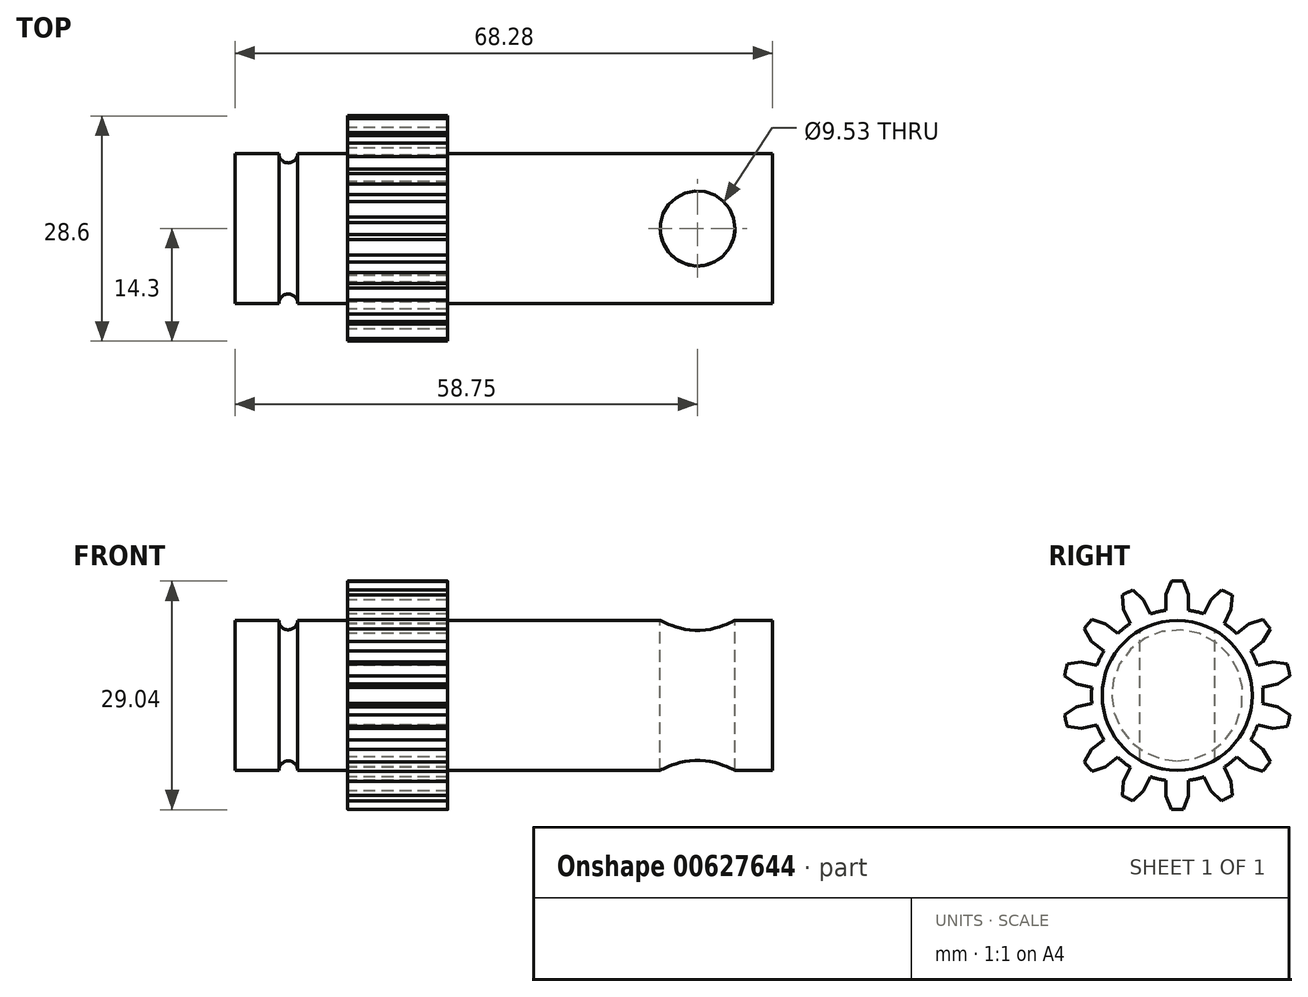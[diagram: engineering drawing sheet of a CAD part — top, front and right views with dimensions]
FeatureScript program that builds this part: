
annotation { "Feature Type Name" : "Feature", "Feature Type Description" : "" }
export const myFeature = defineFeature(function(context is Context, id is Id, definition is map)
    precondition{}
    {
        {
            var Q0;
            Q0=qCreatedBy(makeId("Right.planeOp"),FACE);
            var sketch = newSketch(context, id + "F0", { "sketchPlane" : qUnion([Q0])});
            skCircle(sketch, "E0", {"center": v(0, 0) * mm, "radius": 9.53 * mm});
            skSolve(sketch);
        }
        {
            var Q0;
            Q0 = qSketchRegion(id + "F0", true);
            extrude(context, id + "F1", {"entities" : qUnion([Q0]), "oppositeDirection" : true, "depth" : 14.3 * mm, "offsetDistance" : 25.4 * mm});
        }
        {
            var Q0;
            Q0=makeQuery(id+"F1.opExtrude","CAP_FACE",FACE,{"disambiguationData":[OSD([sQuery(id+"F0.wireOp",EDGE,"E0")])],"isStart":true});
            var sketch = newSketch(context, id + "F2", { "sketchPlane" : qUnion([Q0])});
            skArc(sketch, "E1", {"start": v(0.76, 14.5) * mm, "mid": v(0, 14.52) * mm, "end": v(-0.76, 14.5) * mm});
            skArc(sketch, "E2", {"start": v(-1.41, 10.8) * mm, "mid": v(-2.42, 10.62) * mm, "end": v(-3.41, 10.35) * mm, "construction": true});
            skLineSegment(sketch, "E3", {"start": v(-0.76, 14.5) * mm, "end": v(-1.41, 12.8) * mm});
            skLineSegment(sketch, "E4", {"start": v(-1.41, 12.8) * mm, "end": v(-1.41, 10.8) * mm});
            skLineSegment(sketch, "E5", {"start": v(0, 14.52) * mm, "end": v(0, 10.9) * mm, "construction": true});
            skLineSegment(sketch, "E6.MirrorCS", {"start": v(1.41, 12.8) * mm, "end": v(1.41, 10.8) * mm});
            skLineSegment(sketch, "E7.MirrorCS", {"start": v(0.76, 14.5) * mm, "end": v(1.41, 12.8) * mm});
            skLineSegment(sketch, "E8.1.0", {"start": v(-6.83, 10.92) * mm, "end": v(-5.96, 9.12) * mm});
            skLineSegment(sketch, "E8.1.1", {"start": v(-6.98, 12.73) * mm, "end": v(-6.83, 10.92) * mm});
            skArc(sketch, "E8.1.2", {"start": v(-5.6, 13.4) * mm, "mid": v(-6.3, 13.08) * mm, "end": v(-6.98, 12.73) * mm});
            skLineSegment(sketch, "E8.1.3", {"start": v(-5.6, 13.4) * mm, "end": v(-4.28, 12.14) * mm});
            skLineSegment(sketch, "E8.1.4", {"start": v(-4.28, 12.14) * mm, "end": v(-3.41, 10.35) * mm});
            skLineSegment(sketch, "E8.2.0", {"start": v(-10.89, 6.87) * mm, "end": v(-9.33, 5.63) * mm});
            skLineSegment(sketch, "E8.2.1", {"start": v(-11.8, 8.44) * mm, "end": v(-10.89, 6.87) * mm});
            skArc(sketch, "E8.2.2", {"start": v(-10.86, 9.63) * mm, "mid": v(-11.35, 9.05) * mm, "end": v(-11.8, 8.44) * mm});
            skLineSegment(sketch, "E8.2.3", {"start": v(-10.86, 9.63) * mm, "end": v(-9.13, 9.09) * mm});
            skLineSegment(sketch, "E8.2.4", {"start": v(-9.13, 9.09) * mm, "end": v(-7.57, 7.84) * mm});
            skLineSegment(sketch, "E8.3.0", {"start": v(-12.8, 1.47) * mm, "end": v(-10.85, 1.03) * mm});
            skLineSegment(sketch, "E8.3.1", {"start": v(-14.3, 2.48) * mm, "end": v(-12.8, 1.47) * mm});
            skArc(sketch, "E8.3.2", {"start": v(-13.96, 3.97) * mm, "mid": v(-14.15, 3.23) * mm, "end": v(-14.3, 2.48) * mm});
            skLineSegment(sketch, "E8.3.3", {"start": v(-13.96, 3.97) * mm, "end": v(-12.16, 4.23) * mm});
            skLineSegment(sketch, "E8.3.4", {"start": v(-12.16, 4.23) * mm, "end": v(-10.22, 3.78) * mm});
            skLineSegment(sketch, "E8.4.0", {"start": v(-12.16, -4.23) * mm, "end": v(-10.22, -3.78) * mm});
            skLineSegment(sketch, "E8.4.1", {"start": v(-13.96, -3.97) * mm, "end": v(-12.16, -4.23) * mm});
            skArc(sketch, "E8.4.2", {"start": v(-14.3, -2.48) * mm, "mid": v(-14.15, -3.23) * mm, "end": v(-13.96, -3.97) * mm});
            skLineSegment(sketch, "E8.4.3", {"start": v(-14.3, -2.48) * mm, "end": v(-12.8, -1.47) * mm});
            skLineSegment(sketch, "E8.4.4", {"start": v(-12.8, -1.47) * mm, "end": v(-10.85, -1.03) * mm});
            skLineSegment(sketch, "E8.5.0", {"start": v(-9.13, -9.09) * mm, "end": v(-7.57, -7.84) * mm});
            skLineSegment(sketch, "E8.5.1", {"start": v(-10.86, -9.63) * mm, "end": v(-9.13, -9.09) * mm});
            skArc(sketch, "E8.5.2", {"start": v(-11.8, -8.44) * mm, "mid": v(-11.35, -9.05) * mm, "end": v(-10.86, -9.63) * mm});
            skLineSegment(sketch, "E8.5.3", {"start": v(-11.8, -8.44) * mm, "end": v(-10.89, -6.87) * mm});
            skLineSegment(sketch, "E8.5.4", {"start": v(-10.89, -6.87) * mm, "end": v(-9.33, -5.63) * mm});
            skLineSegment(sketch, "E8.6.0", {"start": v(-4.28, -12.14) * mm, "end": v(-3.41, -10.35) * mm});
            skLineSegment(sketch, "E8.6.1", {"start": v(-5.6, -13.4) * mm, "end": v(-4.28, -12.14) * mm});
            skArc(sketch, "E8.6.2", {"start": v(-6.98, -12.73) * mm, "mid": v(-6.3, -13.08) * mm, "end": v(-5.6, -13.4) * mm});
            skLineSegment(sketch, "E8.6.3", {"start": v(-6.98, -12.73) * mm, "end": v(-6.83, -10.92) * mm});
            skLineSegment(sketch, "E8.6.4", {"start": v(-6.83, -10.92) * mm, "end": v(-5.96, -9.12) * mm});
            skLineSegment(sketch, "E8.7.0", {"start": v(1.41, -12.8) * mm, "end": v(1.41, -10.8) * mm});
            skLineSegment(sketch, "E8.7.1", {"start": v(0.76, -14.5) * mm, "end": v(1.41, -12.8) * mm});
            skArc(sketch, "E8.7.2", {"start": v(-0.76, -14.5) * mm, "mid": v(0, -14.52) * mm, "end": v(0.76, -14.5) * mm});
            skLineSegment(sketch, "E8.7.3", {"start": v(-0.76, -14.5) * mm, "end": v(-1.41, -12.8) * mm});
            skLineSegment(sketch, "E8.7.4", {"start": v(-1.41, -12.8) * mm, "end": v(-1.41, -10.8) * mm});
            skLineSegment(sketch, "E8.8.0", {"start": v(6.83, -10.92) * mm, "end": v(5.96, -9.12) * mm});
            skLineSegment(sketch, "E8.8.1", {"start": v(6.98, -12.73) * mm, "end": v(6.83, -10.92) * mm});
            skArc(sketch, "E8.8.2", {"start": v(5.6, -13.4) * mm, "mid": v(6.3, -13.08) * mm, "end": v(6.98, -12.73) * mm});
            skLineSegment(sketch, "E8.8.3", {"start": v(5.6, -13.4) * mm, "end": v(4.28, -12.14) * mm});
            skLineSegment(sketch, "E8.8.4", {"start": v(4.28, -12.14) * mm, "end": v(3.41, -10.35) * mm});
            skLineSegment(sketch, "E8.9.0", {"start": v(10.89, -6.87) * mm, "end": v(9.33, -5.63) * mm});
            skLineSegment(sketch, "E8.9.1", {"start": v(11.8, -8.44) * mm, "end": v(10.89, -6.87) * mm});
            skArc(sketch, "E8.9.2", {"start": v(10.86, -9.63) * mm, "mid": v(11.35, -9.05) * mm, "end": v(11.8, -8.44) * mm});
            skLineSegment(sketch, "E8.9.3", {"start": v(10.86, -9.63) * mm, "end": v(9.13, -9.09) * mm});
            skLineSegment(sketch, "E8.9.4", {"start": v(9.13, -9.09) * mm, "end": v(7.57, -7.84) * mm});
            skLineSegment(sketch, "E8.10.0", {"start": v(12.8, -1.47) * mm, "end": v(10.85, -1.03) * mm});
            skLineSegment(sketch, "E8.10.1", {"start": v(14.3, -2.48) * mm, "end": v(12.8, -1.47) * mm});
            skArc(sketch, "E8.10.2", {"start": v(13.96, -3.97) * mm, "mid": v(14.15, -3.23) * mm, "end": v(14.3, -2.48) * mm});
            skLineSegment(sketch, "E8.10.3", {"start": v(13.96, -3.97) * mm, "end": v(12.16, -4.23) * mm});
            skLineSegment(sketch, "E8.10.4", {"start": v(12.16, -4.23) * mm, "end": v(10.22, -3.78) * mm});
            skLineSegment(sketch, "E8.11.0", {"start": v(12.16, 4.23) * mm, "end": v(10.22, 3.78) * mm});
            skLineSegment(sketch, "E8.11.1", {"start": v(13.96, 3.97) * mm, "end": v(12.16, 4.23) * mm});
            skArc(sketch, "E8.11.2", {"start": v(14.3, 2.48) * mm, "mid": v(14.15, 3.23) * mm, "end": v(13.96, 3.97) * mm});
            skLineSegment(sketch, "E8.11.3", {"start": v(14.3, 2.48) * mm, "end": v(12.8, 1.47) * mm});
            skLineSegment(sketch, "E8.11.4", {"start": v(12.8, 1.47) * mm, "end": v(10.85, 1.03) * mm});
            skLineSegment(sketch, "E8.12.0", {"start": v(9.13, 9.09) * mm, "end": v(7.57, 7.84) * mm});
            skLineSegment(sketch, "E8.12.1", {"start": v(10.86, 9.63) * mm, "end": v(9.13, 9.09) * mm});
            skArc(sketch, "E8.12.2", {"start": v(11.8, 8.44) * mm, "mid": v(11.35, 9.05) * mm, "end": v(10.86, 9.63) * mm});
            skLineSegment(sketch, "E8.12.3", {"start": v(11.8, 8.44) * mm, "end": v(10.89, 6.87) * mm});
            skLineSegment(sketch, "E8.12.4", {"start": v(10.89, 6.87) * mm, "end": v(9.33, 5.63) * mm});
            skLineSegment(sketch, "E8.13.0", {"start": v(4.28, 12.14) * mm, "end": v(3.41, 10.35) * mm});
            skLineSegment(sketch, "E8.13.1", {"start": v(5.6, 13.4) * mm, "end": v(4.28, 12.14) * mm});
            skArc(sketch, "E8.13.2", {"start": v(6.98, 12.73) * mm, "mid": v(6.3, 13.08) * mm, "end": v(5.6, 13.4) * mm});
            skLineSegment(sketch, "E8.13.3", {"start": v(6.98, 12.73) * mm, "end": v(6.83, 10.92) * mm});
            skLineSegment(sketch, "E8.13.4", {"start": v(6.83, 10.92) * mm, "end": v(5.96, 9.12) * mm});
            skArc(sketch, "E9", {"start": v(-1.41, 10.8) * mm, "mid": v(-2.42, 10.62) * mm, "end": v(-3.41, 10.35) * mm});
            skArc(sketch, "E10.trimOffspring", {"start": v(3.41, 10.35) * mm, "mid": v(2.42, 10.62) * mm, "end": v(1.41, 10.8) * mm, "construction": true});
            skArc(sketch, "E11.trimOffspring", {"start": v(-5.96, 9.12) * mm, "mid": v(-6.8, 8.52) * mm, "end": v(-7.57, 7.84) * mm, "construction": true});
            skArc(sketch, "E12.trimOffspring", {"start": v(-9.33, 5.63) * mm, "mid": v(-9.82, 4.73) * mm, "end": v(-10.22, 3.78) * mm, "construction": true});
            skArc(sketch, "E13.trimOffspring", {"start": v(-5.96, 9.12) * mm, "mid": v(-6.8, 8.52) * mm, "end": v(-7.57, 7.84) * mm});
            skArc(sketch, "E14.trimOffspring", {"start": v(-9.33, 5.63) * mm, "mid": v(-9.82, 4.73) * mm, "end": v(-10.22, 3.78) * mm});
            skArc(sketch, "E15.trimOffspring", {"start": v(3.41, 10.35) * mm, "mid": v(2.42, 10.62) * mm, "end": v(1.41, 10.8) * mm});
            skArc(sketch, "E16.trimOffspring", {"start": v(7.57, 7.84) * mm, "mid": v(6.8, 8.52) * mm, "end": v(5.96, 9.12) * mm, "construction": true});
            skArc(sketch, "E17.trimOffspring", {"start": v(7.57, 7.84) * mm, "mid": v(6.8, 8.52) * mm, "end": v(5.96, 9.12) * mm});
            skArc(sketch, "E18.trimOffspring", {"start": v(10.22, 3.78) * mm, "mid": v(9.82, 4.73) * mm, "end": v(9.33, 5.63) * mm});
            skArc(sketch, "E19.trimOffspring", {"start": v(10.85, -1.03) * mm, "mid": v(10.9, 0) * mm, "end": v(10.85, 1.03) * mm});
            skArc(sketch, "E20.trimOffspring", {"start": v(9.33, -5.63) * mm, "mid": v(9.82, -4.73) * mm, "end": v(10.22, -3.78) * mm, "construction": true});
            skArc(sketch, "E21.trimOffspring", {"start": v(9.33, -5.63) * mm, "mid": v(9.82, -4.73) * mm, "end": v(10.22, -3.78) * mm});
            skArc(sketch, "E22.trimOffspring", {"start": v(5.96, -9.12) * mm, "mid": v(6.8, -8.52) * mm, "end": v(7.57, -7.84) * mm, "construction": true});
            skArc(sketch, "E23.trimOffspring", {"start": v(5.96, -9.12) * mm, "mid": v(6.8, -8.52) * mm, "end": v(7.57, -7.84) * mm});
            skArc(sketch, "E24.trimOffspring", {"start": v(1.41, -10.8) * mm, "mid": v(2.42, -10.62) * mm, "end": v(3.41, -10.35) * mm, "construction": true});
            skArc(sketch, "E25.trimOffspring", {"start": v(1.41, -10.8) * mm, "mid": v(2.42, -10.62) * mm, "end": v(3.41, -10.35) * mm});
            skArc(sketch, "E26.trimOffspring", {"start": v(-3.41, -10.35) * mm, "mid": v(-2.42, -10.62) * mm, "end": v(-1.41, -10.8) * mm, "construction": true});
            skArc(sketch, "E27.trimOffspring", {"start": v(-3.41, -10.35) * mm, "mid": v(-2.42, -10.62) * mm, "end": v(-1.41, -10.8) * mm});
            skArc(sketch, "E28.trimOffspring", {"start": v(-7.57, -7.84) * mm, "mid": v(-6.8, -8.52) * mm, "end": v(-5.96, -9.12) * mm, "construction": true});
            skArc(sketch, "E29.trimOffspring", {"start": v(-7.57, -7.84) * mm, "mid": v(-6.8, -8.52) * mm, "end": v(-5.96, -9.12) * mm});
            skArc(sketch, "E30.trimOffspring", {"start": v(-10.22, -3.78) * mm, "mid": v(-9.82, -4.73) * mm, "end": v(-9.33, -5.63) * mm, "construction": true});
            skArc(sketch, "E31.trimOffspring", {"start": v(-10.22, -3.78) * mm, "mid": v(-9.82, -4.73) * mm, "end": v(-9.33, -5.63) * mm});
            skArc(sketch, "E32.trimOffspring", {"start": v(-10.85, 1.03) * mm, "mid": v(-10.9, 0) * mm, "end": v(-10.85, -1.03) * mm, "construction": true});
            skArc(sketch, "E33.trimOffspring", {"start": v(-10.85, 1.03) * mm, "mid": v(-10.9, 0) * mm, "end": v(-10.85, -1.03) * mm});
            skSolve(sketch);
        }
        {
            var Q0;
            Q0 = qSketchRegion(id + "F2", true);
            extrude(context, id + "F3", {"entities" : qUnion([Q0]), "operationType" : NewBodyOperationType.ADD, "depth" : 12.7 * mm, "offsetDistance" : 25.4 * mm});
        }
        {
            var Q0;
            Q0=makeQuery(id+"F3.opExtrude","CAP_FACE",FACE,{"disambiguationData":[OSD([sQuery(id+"F2.wireOp",EDGE,"E1")])],"isStart":false});
            var sketch = newSketch(context, id + "F4", { "sketchPlane" : qUnion([Q0])});
            skCircle(sketch, "E34", {"center": v(0, 0) * mm, "radius": 9.53 * mm});
            skSolve(sketch);
        }
        {
            var Q0;
            Q0 = qSketchRegion(id + "F4", true);
            extrude(context, id + "F5", {"entities" : qUnion([Q0]), "operationType" : NewBodyOperationType.ADD, "depth" : 41.27 * mm, "offsetDistance" : 25.4 * mm});
        }
        {
            var Q0;
            Q0=qCreatedBy(makeId("Top.planeOp"),FACE);
            var sketch = newSketch(context, id + "F6", { "sketchPlane" : qUnion([Q0])});
            skLineSegment(sketch, "E35", {"start": v(0, 0) * mm, "end": v(-20.93, 0) * mm, "construction": true});
            skCircle(sketch, "E36", {"center": v(-7.54, 9.53) * mm, "radius": 1.2 * mm});
            skSolve(sketch);
        }
        {
            var Q0;
            Q0 = qSketchRegion(id + "F6", true);
            var Q1;
            Q1=sQuery(id+"F6.wireOp",EDGE,"E35");
            revolve(context, id + "F7", {"operationType" : NewBodyOperationType.REMOVE, "entities" : qUnion([Q0]), "axis" : qUnion([Q1]), "revolveType" : RevolveType.FULL, "oppositeDirection" : true});
        }
        {
            var Q0;
            Q0=qCreatedBy(makeId("Top.planeOp"),FACE);
            var sketch = newSketch(context, id + "F8", { "sketchPlane" : qUnion([Q0])});
            skCircle(sketch, "E37", {"center": v(44.45, 0) * mm, "radius": 4.76 * mm});
            skSolve(sketch);
        }
        {
            var Q0;
            Q0 = qSketchRegion(id + "F8", true);
            extrude(context, id + "F9", {"entities" : qUnion([Q0]), "operationType" : NewBodyOperationType.REMOVE, "endBound" : BoundingType.SYMMETRIC, "oppositeDirection" : true, "depth" : 25.4 * mm, "offsetDistance" : 25.4 * mm});
        }
    });
